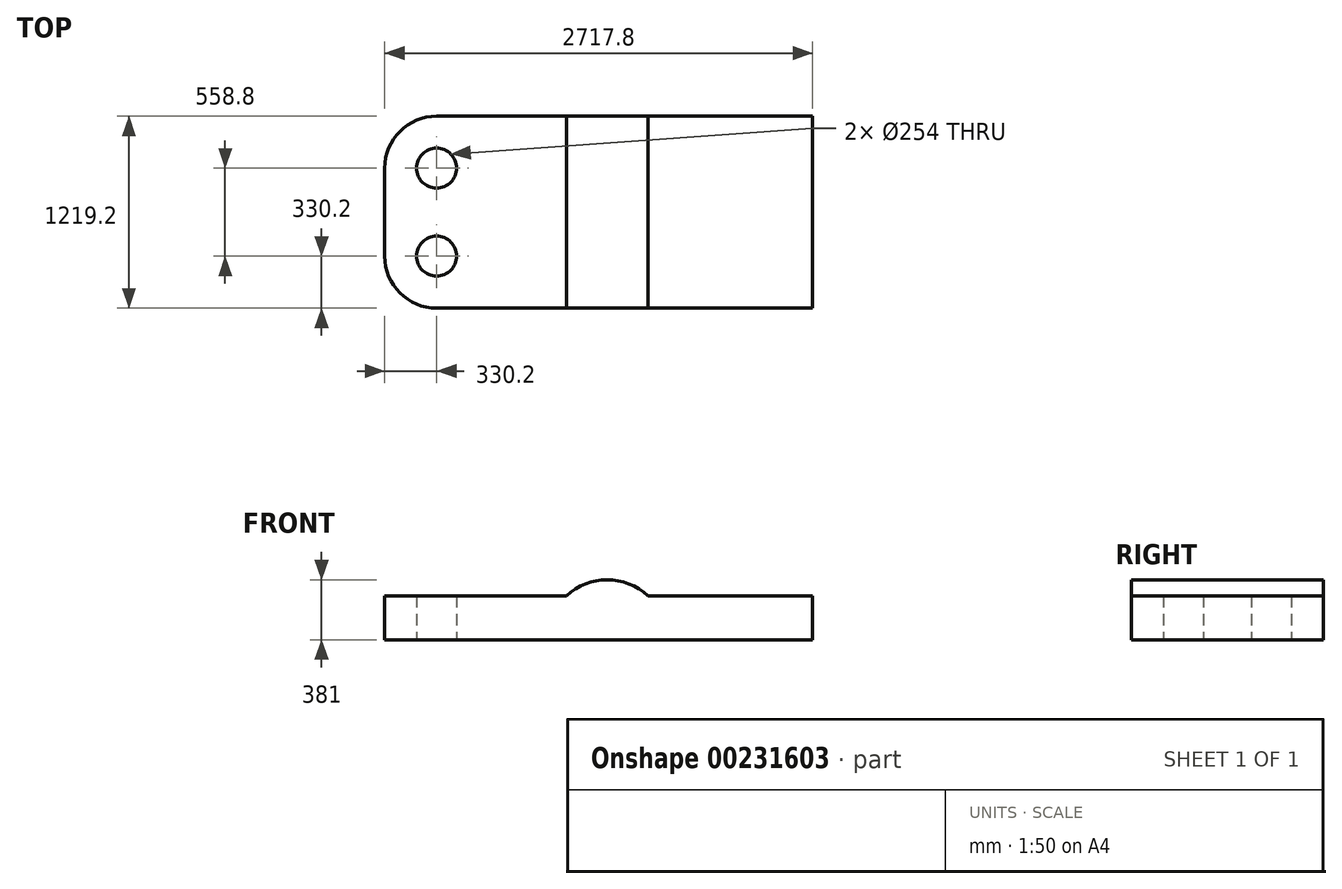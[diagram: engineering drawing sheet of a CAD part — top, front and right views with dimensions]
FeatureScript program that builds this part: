
annotation { "Feature Type Name" : "Feature", "Feature Type Description" : "" }
export const myFeature = defineFeature(function(context is Context, id is Id, definition is map)
    precondition{}
    {
        {
            var Q0;
            Q0=qCreatedBy(makeId("Top.planeOp"),FACE);
            var sketch = newSketch(context, id + "F0", { "sketchPlane" : qUnion([Q0])});
            skLineSegment(sketch, "E0.bottom", {"start": v(-1028.7, -609.6) * mm, "end": v(1358.9, -609.6) * mm});
            skLineSegment(sketch, "E0.top", {"start": v(-1028.7, 609.6) * mm, "end": v(1358.9, 609.6) * mm});
            skLineSegment(sketch, "E0.left", {"start": v(-1358.9, -279.4) * mm, "end": v(-1358.9, 279.4) * mm});
            skLineSegment(sketch, "E0.right", {"start": v(1358.9, -609.6) * mm, "end": v(1358.9, 609.6) * mm});
            skPoint(sketch, "E0.middle", {"position": v(0, 0) * mm});
            skPoint(sketch, "E1.visualSharp", {"position": v(-1358.9, 609.6) * mm});
            skArc(sketch, "E1.filletArc", {"start": v(-1028.7, 609.6) * mm, "mid": v(-1262.19, 512.89) * mm, "end": v(-1358.9, 279.4) * mm});
            skPoint(sketch, "E2.visualSharp", {"position": v(-1358.9, -609.6) * mm});
            skArc(sketch, "E2.filletArc", {"start": v(-1358.9, -279.4) * mm, "mid": v(-1262.19, -512.89) * mm, "end": v(-1028.7, -609.6) * mm});
            skCircle(sketch, "E3", {"center": v(-1028.7, 279.4) * mm, "radius": 127 * mm});
            skCircle(sketch, "E4", {"center": v(-1028.7, -279.4) * mm, "radius": 127 * mm});
            skSolve(sketch);
        }
        {
            var Q0;
            Q0=makeQuery(id+"F0.imprint","IMPRINT",FACE,{"disambiguationData":[TD([[makeQuery(id+"F0.imprint","IMPRINT",EDGE,{"derivedFrom":sQuery(id+"F0.wireOp",EDGE,"E0.bottom")}),1.0]])]});
            extrude(context, id + "F1", {"entities" : qUnion([Q0]), "depth" : 279.4 * mm});
        }
        {
            var Q0;
            Q0=makeQuery(id+"F1.opExtrude","SWEPT_FACE",FACE,{"disambiguationData":[OSD([sQuery(id+"F0.wireOp",EDGE,"E0.bottom")])]});
            var sketch = newSketch(context, id + "F2", { "sketchPlane" : qUnion([Q0])});
            skArc(sketch, "E5", {"start": v(295.6, 0) * mm, "mid": v(54.3, 241.3) * mm, "end": v(-187, 0) * mm});
            skArc(sketch, "E6", {"start": v(435.3, 0) * mm, "mid": v(54.3, 381) * mm, "end": v(-326.7, 0) * mm});
            skSolve(sketch);
        }
        {
            var Q0;
            {var subQ0=sQuery(id+"F2.wireOp",EDGE,"E6");var subQ1=makeQuery(id+"F1.opExtrude","CAP_EDGE",EDGE,{"disambiguationData":[OSD([sQuery(id+"F0.wireOp",EDGE,"E0.bottom")])],"isStart":false});var subQ2=makeQuery(id+"F2.imprint","INTERSECT",VERTEX,{"disambiguationData":[OD(0.0)],"derivedFrom":[subQ1,subQ0]});Q0=makeQuery(id+"F2.imprint","IMPRINT",FACE,{"disambiguationData":[TD([[makeQuery(id+"F2.imprint","IMPRINT",EDGE,{"disambiguationData":[TD([[subQ2,-1.0]])],"derivedFrom":subQ0}),1.0]])]});}
            var Q1;
            {var subQ1=sQuery(id+"F0.wireOp",EDGE,"E0.bottom");var subQ5=makeQuery(id+"F1.opExtrude","CAP_EDGE",EDGE,{"disambiguationData":[OSD([subQ1])],"isStart":true});var subQ8=sQuery(id+"F2.wireOp",EDGE,"E5");var subQ9=makeQuery(id+"F2.imprint","INTERSECT",VERTEX,{"disambiguationData":[OD(0.0)],"derivedFrom":[subQ5,subQ8]});Q1=makeQuery(id+"F2.imprint","IMPRINT",FACE,{"disambiguationData":[TD([[makeQuery(id+"F2.imprint","IMPRINT",EDGE,{"disambiguationData":[TD([[subQ9,-1.0]])],"derivedFrom":subQ8}),-1.0]])]});}
            extrude(context, id + "F3", {"entities" : qUnion([Q0, Q1]), "operationType" : NewBodyOperationType.ADD, "oppositeDirection" : true, "depth" : 1219.2 * mm});
        }
    });
